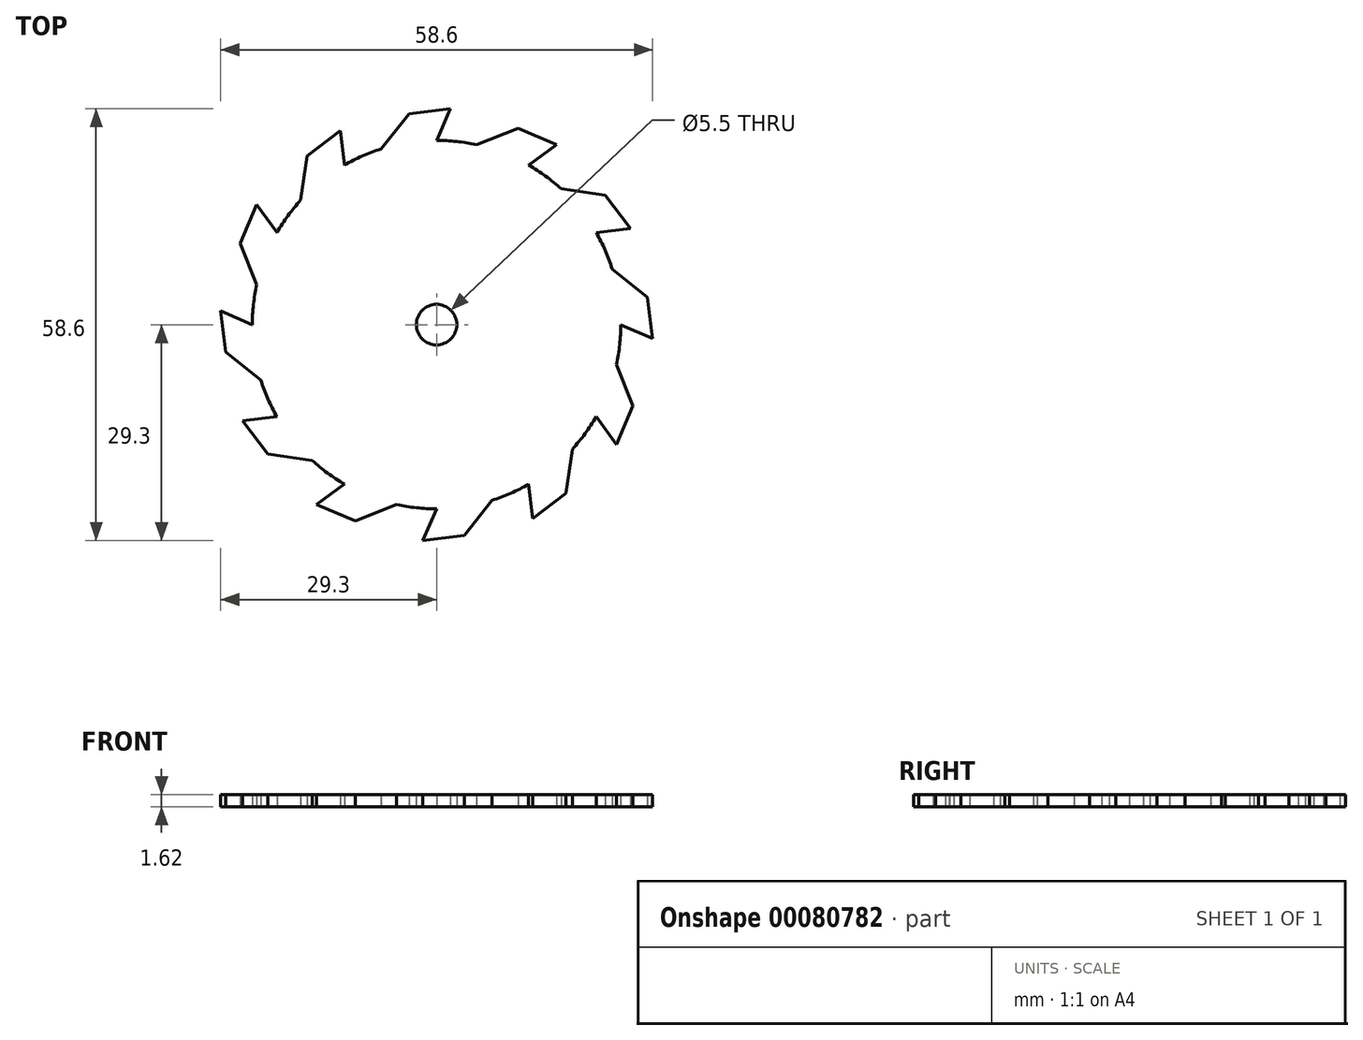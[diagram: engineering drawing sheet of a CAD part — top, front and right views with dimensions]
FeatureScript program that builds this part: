
annotation { "Feature Type Name" : "Feature", "Feature Type Description" : "" }
export const myFeature = defineFeature(function(context is Context, id is Id, definition is map)
    precondition{}
    {
        {
            var Q0;
            Q0=qCreatedBy(makeId("Top.planeOp"),FACE);
            var sketch = newSketch(context, id + "F0", { "sketchPlane" : qUnion([Q0])});
            skCircle(sketch, "E0", {"center": v(0, 0) * mm, "radius": 25 * mm});
            skCircle(sketch, "E1", {"center": v(0, 0) * mm, "radius": 2.75 * mm});
            skLineSegment(sketch, "E2", {"start": v(-7.5, 23.85) * mm, "end": v(-3.75, 28.59) * mm});
            skLineSegment(sketch, "E3", {"start": v(-3.75, 28.59) * mm, "end": v(1.88, 29.3) * mm});
            skLineSegment(sketch, "E4", {"start": v(1.88, 29.3) * mm, "end": v(0, 25) * mm});
            skLineSegment(sketch, "E5.1.0", {"start": v(-17.54, 22.88) * mm, "end": v(-13.02, 26.31) * mm});
            skLineSegment(sketch, "E5.1.1", {"start": v(-18.43, 16.9) * mm, "end": v(-17.54, 22.88) * mm});
            skLineSegment(sketch, "E5.1.2", {"start": v(-13.02, 26.31) * mm, "end": v(-12.5, 21.65) * mm});
            skLineSegment(sketch, "E5.2.0", {"start": v(-26.63, 11.05) * mm, "end": v(-24.44, 16.27) * mm});
            skLineSegment(sketch, "E5.2.1", {"start": v(-24.4, 5.42) * mm, "end": v(-26.63, 11.05) * mm});
            skLineSegment(sketch, "E5.2.2", {"start": v(-24.44, 16.27) * mm, "end": v(-21.65, 12.5) * mm});
            skLineSegment(sketch, "E5.3.0", {"start": v(-28.59, -3.75) * mm, "end": v(-29.3, 1.88) * mm});
            skLineSegment(sketch, "E5.3.1", {"start": v(-23.85, -7.5) * mm, "end": v(-28.59, -3.75) * mm});
            skLineSegment(sketch, "E5.3.2", {"start": v(-29.3, 1.88) * mm, "end": v(-25, 0) * mm});
            skLineSegment(sketch, "E5.4.0", {"start": v(-22.88, -17.54) * mm, "end": v(-26.31, -13.02) * mm});
            skLineSegment(sketch, "E5.4.1", {"start": v(-16.9, -18.43) * mm, "end": v(-22.88, -17.54) * mm});
            skLineSegment(sketch, "E5.4.2", {"start": v(-26.31, -13.02) * mm, "end": v(-21.65, -12.5) * mm});
            skLineSegment(sketch, "E5.5.0", {"start": v(-11.05, -26.63) * mm, "end": v(-16.27, -24.44) * mm});
            skLineSegment(sketch, "E5.5.1", {"start": v(-5.42, -24.4) * mm, "end": v(-11.05, -26.63) * mm});
            skLineSegment(sketch, "E5.5.2", {"start": v(-16.27, -24.44) * mm, "end": v(-12.5, -21.65) * mm});
            skLineSegment(sketch, "E5.6.0", {"start": v(3.75, -28.59) * mm, "end": v(-1.88, -29.3) * mm});
            skLineSegment(sketch, "E5.6.1", {"start": v(7.5, -23.85) * mm, "end": v(3.75, -28.59) * mm});
            skLineSegment(sketch, "E5.6.2", {"start": v(-1.88, -29.3) * mm, "end": v(0, -25) * mm});
            skLineSegment(sketch, "E5.7.0", {"start": v(17.54, -22.88) * mm, "end": v(13.02, -26.31) * mm});
            skLineSegment(sketch, "E5.7.1", {"start": v(18.43, -16.9) * mm, "end": v(17.54, -22.88) * mm});
            skLineSegment(sketch, "E5.7.2", {"start": v(13.02, -26.31) * mm, "end": v(12.5, -21.65) * mm});
            skLineSegment(sketch, "E5.8.0", {"start": v(26.63, -11.05) * mm, "end": v(24.44, -16.27) * mm});
            skLineSegment(sketch, "E5.8.1", {"start": v(24.4, -5.42) * mm, "end": v(26.63, -11.05) * mm});
            skLineSegment(sketch, "E5.8.2", {"start": v(24.44, -16.27) * mm, "end": v(21.65, -12.5) * mm});
            skLineSegment(sketch, "E5.9.0", {"start": v(28.59, 3.75) * mm, "end": v(29.3, -1.88) * mm});
            skLineSegment(sketch, "E5.9.1", {"start": v(23.85, 7.5) * mm, "end": v(28.59, 3.75) * mm});
            skLineSegment(sketch, "E5.9.2", {"start": v(29.3, -1.88) * mm, "end": v(25, 0) * mm});
            skLineSegment(sketch, "E6.1.10.0", {"start": v(22.88, 17.54) * mm, "end": v(26.31, 13.02) * mm});
            skLineSegment(sketch, "E6.3.10.0", {"start": v(16.9, 18.43) * mm, "end": v(22.88, 17.54) * mm});
            skLineSegment(sketch, "E6.6.10.0", {"start": v(26.31, 13.02) * mm, "end": v(21.65, 12.5) * mm});
            skLineSegment(sketch, "E6.1.11.0", {"start": v(11.05, 26.63) * mm, "end": v(16.27, 24.44) * mm});
            skLineSegment(sketch, "E6.3.11.0", {"start": v(5.42, 24.4) * mm, "end": v(11.05, 26.63) * mm});
            skLineSegment(sketch, "E6.6.11.0", {"start": v(16.27, 24.44) * mm, "end": v(12.5, 21.65) * mm});
            skSolve(sketch);
        }
        {
            var Q0;
            Q0=makeQuery(id+"F0.imprint","IMPRINT",FACE,{"disambiguationData":[TD([[makeQuery(id+"F0.imprint","IMPRINT",EDGE,{"derivedFrom":sQuery(id+"F0.wireOp",EDGE,"E1")}),-1.0]])]});
            var Q1;
            {var subQ0=sQuery(id+"F0.wireOp",EDGE,"E2");Q1=makeQuery(id+"F0.imprint","IMPRINT",FACE,{"disambiguationData":[TD([[makeQuery(id+"F0.imprint","IMPRINT",EDGE,{"derivedFrom":subQ0}),-1.0]])]});}
            var Q2;
            Q2=makeQuery(id+"F0.imprint","IMPRINT",FACE,{"disambiguationData":[TD([[makeQuery(id+"F0.imprint","IMPRINT",EDGE,{"derivedFrom":sQuery(id+"F0.wireOp",EDGE,"E5.1.0")}),-1.0]])]});
            var Q3;
            Q3=makeQuery(id+"F0.imprint","IMPRINT",FACE,{"disambiguationData":[TD([[makeQuery(id+"F0.imprint","IMPRINT",EDGE,{"derivedFrom":sQuery(id+"F0.wireOp",EDGE,"E5.2.0")}),-1.0]])]});
            var Q4;
            Q4=makeQuery(id+"F0.imprint","IMPRINT",FACE,{"disambiguationData":[TD([[makeQuery(id+"F0.imprint","IMPRINT",EDGE,{"derivedFrom":sQuery(id+"F0.wireOp",EDGE,"E5.3.0")}),-1.0]])]});
            var Q5;
            Q5=makeQuery(id+"F0.imprint","IMPRINT",FACE,{"disambiguationData":[TD([[makeQuery(id+"F0.imprint","IMPRINT",EDGE,{"derivedFrom":sQuery(id+"F0.wireOp",EDGE,"E5.9.0")}),-1.0]])]});
            var Q6;
            Q6=makeQuery(id+"F0.imprint","IMPRINT",FACE,{"disambiguationData":[TD([[makeQuery(id+"F0.imprint","IMPRINT",EDGE,{"derivedFrom":sQuery(id+"F0.wireOp",EDGE,"E5.8.0")}),-1.0]])]});
            var Q7;
            Q7=makeQuery(id+"F0.imprint","IMPRINT",FACE,{"disambiguationData":[TD([[makeQuery(id+"F0.imprint","IMPRINT",EDGE,{"derivedFrom":sQuery(id+"F0.wireOp",EDGE,"E5.4.0")}),-1.0]])]});
            var Q8;
            Q8=makeQuery(id+"F0.imprint","IMPRINT",FACE,{"disambiguationData":[TD([[makeQuery(id+"F0.imprint","IMPRINT",EDGE,{"derivedFrom":sQuery(id+"F0.wireOp",EDGE,"E5.5.0")}),-1.0]])]});
            var Q9;
            Q9=makeQuery(id+"F0.imprint","IMPRINT",FACE,{"disambiguationData":[TD([[makeQuery(id+"F0.imprint","IMPRINT",EDGE,{"derivedFrom":sQuery(id+"F0.wireOp",EDGE,"E5.6.0")}),-1.0]])]});
            var Q10;
            Q10=makeQuery(id+"F0.imprint","IMPRINT",FACE,{"disambiguationData":[TD([[makeQuery(id+"F0.imprint","IMPRINT",EDGE,{"derivedFrom":sQuery(id+"F0.wireOp",EDGE,"E5.7.0")}),-1.0]])]});
            var Q11;
            Q11=makeQuery(id+"F0.imprint","IMPRINT",FACE,{"disambiguationData":[TD([[makeQuery(id+"F0.imprint","IMPRINT",EDGE,{"derivedFrom":sQuery(id+"F0.wireOp",EDGE,"E6.1.11.0")}),-1.0]])]});
            var Q12;
            Q12=makeQuery(id+"F0.imprint","IMPRINT",FACE,{"disambiguationData":[TD([[makeQuery(id+"F0.imprint","IMPRINT",EDGE,{"derivedFrom":sQuery(id+"F0.wireOp",EDGE,"E6.1.10.0")}),-1.0]])]});
            extrude(context, id + "F1", {"entities" : qUnion([Q0, Q1, Q2, Q3, Q4, Q5, Q6, Q7, Q8, Q9, Q10, Q11, Q12]), "depth" : 1.62 * mm});
        }
    });
